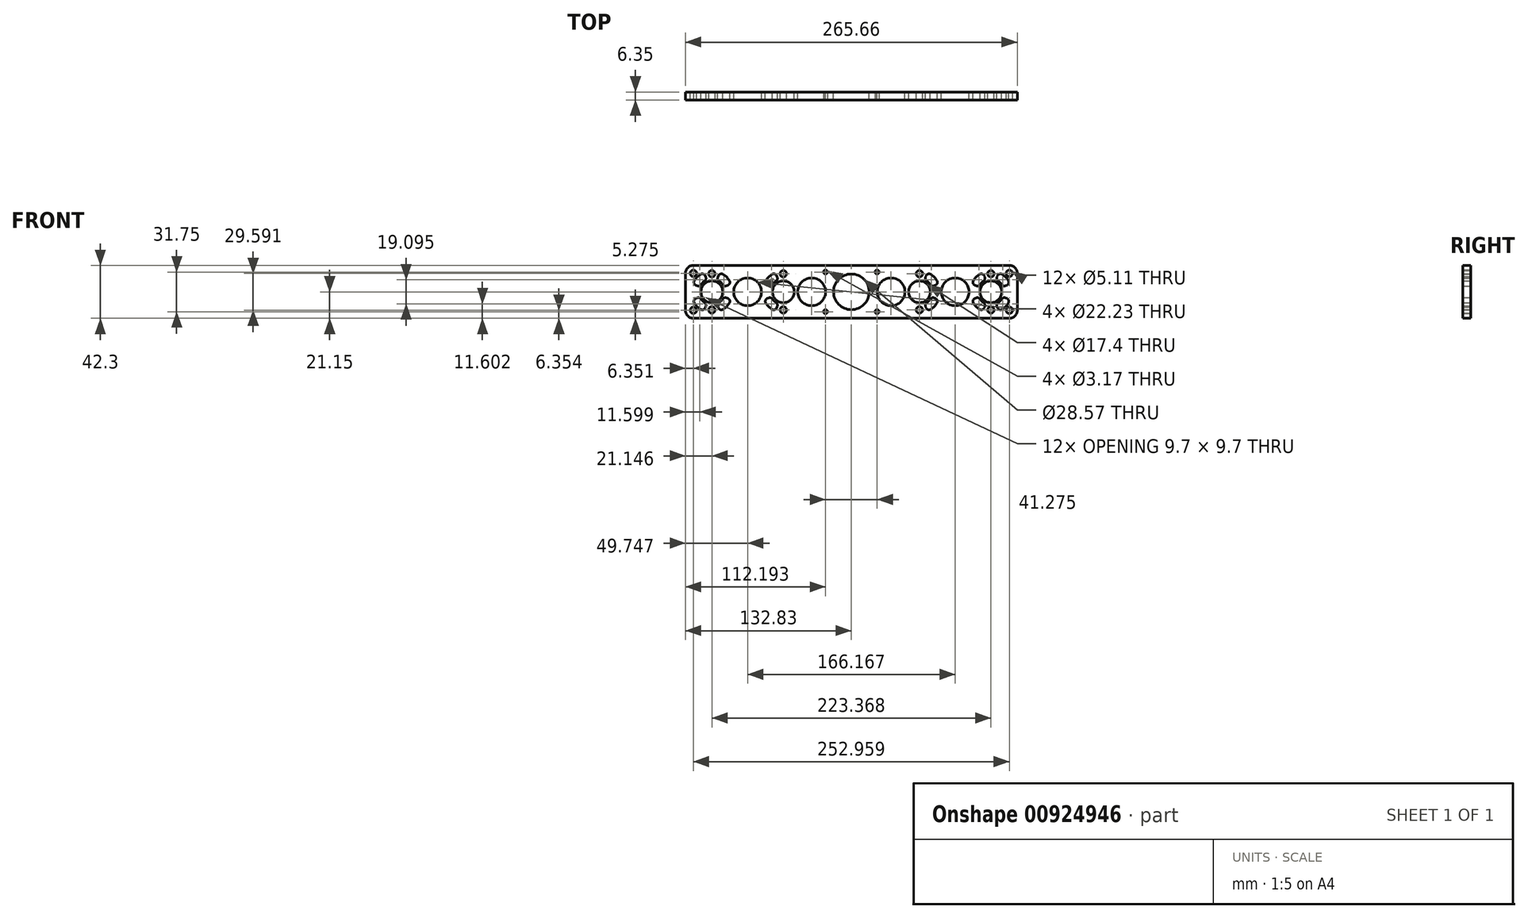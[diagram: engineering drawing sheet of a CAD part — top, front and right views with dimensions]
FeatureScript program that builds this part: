
annotation { "Feature Type Name" : "Feature", "Feature Type Description" : "" }
export const myFeature = defineFeature(function(context is Context, id is Id, definition is map)
    precondition{}
    {
        {
            var Q0;
            Q0=qCreatedBy(makeId("Front.planeOp"),FACE);
            var sketch = newSketch(context, id + "F0", { "sketchPlane" : qUnion([Q0])});
            skLineSegment(sketch, "E0.bottom", {"start": v(-139.7, 25.4) * mm, "end": v(139.7, 25.4) * mm, "construction": true});
            skLineSegment(sketch, "E0.top", {"start": v(-139.7, -25.4) * mm, "end": v(139.7, -25.4) * mm, "construction": true});
            skLineSegment(sketch, "E0.left", {"start": v(-139.7, 25.4) * mm, "end": v(-139.7, -25.4) * mm, "construction": true});
            skLineSegment(sketch, "E0.right", {"start": v(139.7, 25.4) * mm, "end": v(139.7, -25.4) * mm, "construction": true});
            skPoint(sketch, "E0.middle", {"position": v(0, 0) * mm});
            skCircle(sketch, "E1", {"center": v(-111.68, 0) * mm, "radius": 21.15 * mm, "construction": true});
            skCircle(sketch, "E2", {"center": v(-54.48, 0) * mm, "radius": 21.15 * mm, "construction": true});
            skCircle(sketch, "E3", {"center": v(-111.68, 0) * mm, "radius": 4.78 * mm, "construction": true});
            skCircle(sketch, "E4", {"center": v(-83.08, 0) * mm, "radius": 23.83 * mm, "construction": true});
            skCircle(sketch, "E5", {"center": v(-54.48, 0) * mm, "radius": 4.78 * mm, "construction": true});
            skCircle(sketch, "E6", {"center": v(-83.08, 0) * mm, "radius": 19.09 * mm, "construction": true});
            skCircle(sketch, "E7", {"center": v(-31.78, 0) * mm, "radius": 19.09 * mm, "construction": true});
            skCircle(sketch, "E8", {"center": v(-83.08, 0) * mm, "radius": 11.11 * mm});
            skCircle(sketch, "E9", {"center": v(-31.78, 0) * mm, "radius": 8.9 * mm, "construction": true});
            skCircle(sketch, "E10", {"center": v(0, 0) * mm, "radius": 22.87 * mm, "construction": true});
            skLineSegment(sketch, "E11", {"start": v(0, 25.4) * mm, "end": v(0, -25.4) * mm, "construction": true});
            skCircle(sketch, "E12.MirrorC", {"center": v(54.48, 0) * mm, "radius": 21.15 * mm, "construction": true});
            skCircle(sketch, "E13.MirrorC", {"center": v(111.68, 0) * mm, "radius": 21.15 * mm, "construction": true});
            skCircle(sketch, "E14.MirrorC", {"center": v(111.68, 0) * mm, "radius": 4.78 * mm, "construction": true});
            skCircle(sketch, "E15.MirrorC", {"center": v(83.08, 0) * mm, "radius": 19.09 * mm, "construction": true});
            skCircle(sketch, "E16.MirrorC", {"center": v(83.08, 0) * mm, "radius": 11.11 * mm});
            skCircle(sketch, "E17.MirrorC", {"center": v(54.48, 0) * mm, "radius": 4.78 * mm, "construction": true});
            skCircle(sketch, "E18.MirrorC", {"center": v(83.08, 0) * mm, "radius": 23.83 * mm, "construction": true});
            skCircle(sketch, "E19.MirrorC", {"center": v(31.78, 0) * mm, "radius": 19.09 * mm, "construction": true});
            skCircle(sketch, "E20.MirrorC", {"center": v(31.78, 0) * mm, "radius": 8.9 * mm, "construction": true});
            skLineSegment(sketch, "E21", {"start": v(-111.68, 14.5) * mm, "end": v(-111.68, 0) * mm, "construction": true});
            skLineSegment(sketch, "E22", {"start": v(-111.68, 0) * mm, "end": v(-111.68, -14.5) * mm, "construction": true});
            skCircle(sketch, "E23", {"center": v(-111.68, 14.5) * mm, "radius": 2.55 * mm});
            skCircle(sketch, "E24", {"center": v(-111.68, -14.5) * mm, "radius": 2.55 * mm});
            skCircle(sketch, "E25", {"center": v(-111.68, 0) * mm, "radius": 8.7 * mm});
            skLineSegment(sketch, "E26", {"start": v(-54.48, -14.5) * mm, "end": v(-54.48, 0) * mm, "construction": true});
            skLineSegment(sketch, "E27", {"start": v(-54.48, 0) * mm, "end": v(-54.48, 14.5) * mm, "construction": true});
            skCircle(sketch, "E28", {"center": v(-54.48, 14.5) * mm, "radius": 2.55 * mm});
            skCircle(sketch, "E29", {"center": v(-54.48, -14.5) * mm, "radius": 2.55 * mm});
            skCircle(sketch, "E30", {"center": v(-54.48, 0) * mm, "radius": 8.7 * mm});
            skLineSegment(sketch, "E31.MirrorCS", {"start": v(54.48, 0) * mm, "end": v(54.48, 14.5) * mm, "construction": true});
            skCircle(sketch, "E32.MirrorC", {"center": v(54.48, 14.5) * mm, "radius": 2.55 * mm});
            skLineSegment(sketch, "E33.MirrorCS", {"start": v(54.48, -14.5) * mm, "end": v(54.48, 0) * mm, "construction": true});
            skCircle(sketch, "E34.MirrorC", {"center": v(54.48, -14.5) * mm, "radius": 2.55 * mm});
            skCircle(sketch, "E35.MirrorC", {"center": v(54.48, 0) * mm, "radius": 8.7 * mm});
            skCircle(sketch, "E36.MirrorC", {"center": v(111.68, 0) * mm, "radius": 8.7 * mm});
            skLineSegment(sketch, "E37.MirrorCS", {"start": v(111.68, 0) * mm, "end": v(111.68, -14.5) * mm, "construction": true});
            skCircle(sketch, "E38.MirrorC", {"center": v(111.68, -14.5) * mm, "radius": 2.55 * mm});
            skLineSegment(sketch, "E39.MirrorCS", {"start": v(111.68, 14.5) * mm, "end": v(111.68, 0) * mm, "construction": true});
            skCircle(sketch, "E40.MirrorC", {"center": v(111.68, 14.5) * mm, "radius": 2.55 * mm});
            skCircle(sketch, "E41", {"center": v(-31.78, 0) * mm, "radius": 11.11 * mm});
            skCircle(sketch, "E42", {"center": v(31.78, 0) * mm, "radius": 11.11 * mm});
            skCircle(sketch, "E43", {"center": v(0, 0) * mm, "radius": 14.29 * mm});
            skArc(sketch, "E44", {"start": v(-111.68, 21.15) * mm, "mid": v(-132.83, 0) * mm, "end": v(-111.68, -21.15) * mm, "construction": true});
            skLineSegment(sketch, "E45", {"start": v(-111.68, 21.15) * mm, "end": v(111.68, 21.15) * mm});
            skArc(sketch, "E46", {"start": v(111.68, 21.15) * mm, "mid": v(132.83, 0) * mm, "end": v(111.68, -21.15) * mm, "construction": true});
            skLineSegment(sketch, "E47", {"start": v(111.68, -21.15) * mm, "end": v(-111.68, -21.15) * mm});
            skLineSegment(sketch, "E48", {"start": v(111.68, 21.15) * mm, "end": v(126.48, 21.15) * mm});
            skPoint(sketch, "E48.endSnap0", {"position": v(132.83, 0) * mm});
            skLineSegment(sketch, "E49", {"start": v(132.83, 14.8) * mm, "end": v(132.83, -14.8) * mm});
            skLineSegment(sketch, "E50", {"start": v(126.48, -21.15) * mm, "end": v(111.68, -21.15) * mm});
            skCircle(sketch, "E51", {"center": v(126.48, 14.8) * mm, "radius": 6.35 * mm, "construction": true});
            skCircle(sketch, "E52", {"center": v(126.48, 14.8) * mm, "radius": 2.55 * mm});
            skLineSegment(sketch, "E53", {"start": v(-111.68, -21.15) * mm, "end": v(-126.48, -21.15) * mm});
            skPoint(sketch, "E53.endSnap0", {"position": v(-132.83, 0) * mm});
            skLineSegment(sketch, "E54", {"start": v(-132.83, -14.8) * mm, "end": v(-132.83, 14.8) * mm});
            skLineSegment(sketch, "E55", {"start": v(-126.48, 21.15) * mm, "end": v(-111.68, 21.15) * mm});
            skPoint(sketch, "E56.visualSharp", {"position": v(132.83, 21.15) * mm});
            skArc(sketch, "E56.filletArc", {"start": v(132.83, 14.8) * mm, "mid": v(130.97, 19.29) * mm, "end": v(126.48, 21.15) * mm});
            skPoint(sketch, "E57.visualSharp", {"position": v(132.83, -21.15) * mm});
            skArc(sketch, "E57.filletArc", {"start": v(126.48, -21.15) * mm, "mid": v(130.97, -19.29) * mm, "end": v(132.83, -14.8) * mm});
            skPoint(sketch, "E58.visualSharp", {"position": v(-132.83, -21.15) * mm});
            skArc(sketch, "E58.filletArc", {"start": v(-132.83, -14.8) * mm, "mid": v(-130.97, -19.29) * mm, "end": v(-126.48, -21.15) * mm});
            skPoint(sketch, "E59.visualSharp", {"position": v(-132.83, 21.15) * mm});
            skArc(sketch, "E59.filletArc", {"start": v(-126.48, 21.15) * mm, "mid": v(-130.97, 19.29) * mm, "end": v(-132.83, 14.8) * mm});
            skCircle(sketch, "E60", {"center": v(-126.48, 14.8) * mm, "radius": 6.35 * mm, "construction": true});
            skCircle(sketch, "E61", {"center": v(126.48, -14.8) * mm, "radius": 6.35 * mm, "construction": true});
            skCircle(sketch, "E62", {"center": v(126.48, -14.8) * mm, "radius": 2.55 * mm});
            skCircle(sketch, "E63", {"center": v(-126.48, -14.8) * mm, "radius": 6.35 * mm, "construction": true});
            skCircle(sketch, "E64", {"center": v(-126.48, -14.8) * mm, "radius": 2.55 * mm});
            skCircle(sketch, "E65", {"center": v(-126.48, 14.8) * mm, "radius": 2.55 * mm});
            skSolve(sketch);
        }
        {
            var Q0;
            Q0 = qSketchRegion(id + "F0", true);
            extrude(context, id + "F1", {"entities" : qUnion([Q0]), "depth" : 6.35 * mm, "offsetDistance" : 25.4 * mm});
        }
        {
            var Q0;
            Q0=makeQuery(id+"F1.opExtrude","CAP_FACE",FACE,{"disambiguationData":[OSD([sQuery(id+"F0.wireOp",EDGE,"E8"),sQuery(id+"F0.wireOp",EDGE,"E16.MirrorC"),sQuery(id+"F0.wireOp",EDGE,"E23"),sQuery(id+"F0.wireOp",EDGE,"E24"),sQuery(id+"F0.wireOp",EDGE,"E25"),sQuery(id+"F0.wireOp",EDGE,"E28"),sQuery(id+"F0.wireOp",EDGE,"E29"),sQuery(id+"F0.wireOp",EDGE,"E30"),sQuery(id+"F0.wireOp",EDGE,"E32.MirrorC"),sQuery(id+"F0.wireOp",EDGE,"E34.MirrorC"),sQuery(id+"F0.wireOp",EDGE,"E35.MirrorC"),sQuery(id+"F0.wireOp",EDGE,"E36.MirrorC"),sQuery(id+"F0.wireOp",EDGE,"E38.MirrorC"),sQuery(id+"F0.wireOp",EDGE,"E40.MirrorC"),sQuery(id+"F0.wireOp",EDGE,"E41"),sQuery(id+"F0.wireOp",EDGE,"E42"),sQuery(id+"F0.wireOp",EDGE,"E43"),sQuery(id+"F0.wireOp",EDGE,"E44"),sQuery(id+"F0.wireOp",EDGE,"E45"),sQuery(id+"F0.wireOp",EDGE,"E46"),sQuery(id+"F0.wireOp",EDGE,"E47")])],"isStart":false});
            var sketch = newSketch(context, id + "F2", { "sketchPlane" : qUnion([Q0])});
            skLineSegment(sketch, "E66.bottom", {"start": v(20.64, 15.88) * mm, "end": v(-20.64, 15.88) * mm, "construction": true});
            skLineSegment(sketch, "E66.top", {"start": v(20.64, -15.88) * mm, "end": v(-20.64, -15.88) * mm, "construction": true});
            skLineSegment(sketch, "E66.left", {"start": v(20.64, 15.88) * mm, "end": v(20.64, -15.88) * mm, "construction": true});
            skLineSegment(sketch, "E66.right", {"start": v(-20.64, 15.88) * mm, "end": v(-20.64, -15.88) * mm, "construction": true});
            skPoint(sketch, "E66.middle", {"position": v(0, 0) * mm});
            skCircle(sketch, "E67", {"center": v(20.64, 15.88) * mm, "radius": 1.59 * mm});
            skCircle(sketch, "E68", {"center": v(20.64, -15.88) * mm, "radius": 1.59 * mm});
            skCircle(sketch, "E69", {"center": v(-20.64, -15.88) * mm, "radius": 1.59 * mm});
            skCircle(sketch, "E70", {"center": v(-20.64, 15.88) * mm, "radius": 1.59 * mm});
            skSolve(sketch);
        }
        {
            var Q0;
            Q0 = qSketchRegion(id + "F2", true);
            extrude(context, id + "F3", {"entities" : qUnion([Q0]), "operationType" : NewBodyOperationType.REMOVE, "endBound" : BoundingType.THROUGH_ALL, "oppositeDirection" : true, "depth" : 25.4 * mm, "offsetDistance" : 25.4 * mm});
        }
        {
            var Q0;
            Q0=makeQuery(id+"F1.opExtrude","CAP_FACE",FACE,{"disambiguationData":[OSD([sQuery(id+"F0.wireOp",EDGE,"E8"),sQuery(id+"F0.wireOp",EDGE,"E16.MirrorC"),sQuery(id+"F0.wireOp",EDGE,"E23"),sQuery(id+"F0.wireOp",EDGE,"E24"),sQuery(id+"F0.wireOp",EDGE,"E25"),sQuery(id+"F0.wireOp",EDGE,"E28"),sQuery(id+"F0.wireOp",EDGE,"E29"),sQuery(id+"F0.wireOp",EDGE,"E30"),sQuery(id+"F0.wireOp",EDGE,"E32.MirrorC"),sQuery(id+"F0.wireOp",EDGE,"E34.MirrorC"),sQuery(id+"F0.wireOp",EDGE,"E35.MirrorC"),sQuery(id+"F0.wireOp",EDGE,"E36.MirrorC"),sQuery(id+"F0.wireOp",EDGE,"E38.MirrorC"),sQuery(id+"F0.wireOp",EDGE,"E40.MirrorC"),sQuery(id+"F0.wireOp",EDGE,"E41"),sQuery(id+"F0.wireOp",EDGE,"E42"),sQuery(id+"F0.wireOp",EDGE,"E43"),sQuery(id+"F0.wireOp",EDGE,"E45"),sQuery(id+"F0.wireOp",EDGE,"E47"),sQuery(id+"F0.wireOp",EDGE,"E48"),sQuery(id+"F0.wireOp",EDGE,"E49"),sQuery(id+"F0.wireOp",EDGE,"E50"),sQuery(id+"F0.wireOp",EDGE,"E52"),sQuery(id+"F0.wireOp",EDGE,"E53"),sQuery(id+"F0.wireOp",EDGE,"E54"),sQuery(id+"F0.wireOp",EDGE,"E55"),sQuery(id+"F0.wireOp",EDGE,"E56.filletArc"),sQuery(id+"F0.wireOp",EDGE,"E57.filletArc"),sQuery(id+"F0.wireOp",EDGE,"E58.filletArc"),sQuery(id+"F0.wireOp",EDGE,"E59.filletArc"),sQuery(id+"F0.wireOp",EDGE,"E62"),sQuery(id+"F0.wireOp",EDGE,"E64"),sQuery(id+"F0.wireOp",EDGE,"E65")])],"isStart":true});
            var sketch = newSketch(context, id + "F4", { "sketchPlane" : qUnion([Q0])});
            skCircle(sketch, "E71", {"center": v(111.68, 0) * mm, "radius": 10.48 * mm, "construction": true});
            skCircle(sketch, "E72", {"center": v(111.68, 0) * mm, "radius": 16.67 * mm, "construction": true});
            skLineSegment(sketch, "E73", {"start": v(118.06, 15.4) * mm, "end": v(105.3, -15.4) * mm, "construction": true});
            skLineSegment(sketch, "E74", {"start": v(105.3, 15.4) * mm, "end": v(118.06, -15.4) * mm, "construction": true});
            skLineSegment(sketch, "E75", {"start": v(96.28, 6.38) * mm, "end": v(127.08, -6.38) * mm, "construction": true});
            skLineSegment(sketch, "E76", {"start": v(127.08, 6.38) * mm, "end": v(96.28, -6.38) * mm, "construction": true});
            skLineSegment(sketch, "E77", {"start": v(95.02, 0) * mm, "end": v(128.35, 0) * mm, "construction": true});
            skLineSegment(sketch, "E78", {"start": v(106.8, -11.8) * mm, "end": v(106.37, -12.84) * mm});
            skLineSegment(sketch, "E79", {"start": v(99.89, -4.89) * mm, "end": v(98.84, -5.32) * mm});
            skLineSegment(sketch, "E80", {"start": v(99.89, 4.89) * mm, "end": v(98.84, 5.32) * mm});
            skLineSegment(sketch, "E81", {"start": v(106.8, 11.8) * mm, "end": v(106.37, 12.84) * mm});
            skLineSegment(sketch, "E82", {"start": v(116.57, 11.8) * mm, "end": v(117, 12.84) * mm});
            skLineSegment(sketch, "E83", {"start": v(123.48, 4.89) * mm, "end": v(124.52, 5.32) * mm});
            skLineSegment(sketch, "E84", {"start": v(122.16, 0) * mm, "end": v(128.35, 0) * mm});
            skLineSegment(sketch, "E85", {"start": v(123.48, -4.89) * mm, "end": v(124.52, -5.32) * mm});
            skLineSegment(sketch, "E86", {"start": v(116.57, -11.8) * mm, "end": v(117, -12.84) * mm});
            skArc(sketch, "E87", {"start": v(120.73, -14) * mm, "mid": v(123.47, -11.79) * mm, "end": v(125.69, -9.04) * mm});
            skArc(sketch, "E88", {"start": v(125.69, 9.04) * mm, "mid": v(123.47, 11.79) * mm, "end": v(120.73, 14) * mm});
            skArc(sketch, "E89", {"start": v(102.64, 14) * mm, "mid": v(99.9, 11.79) * mm, "end": v(97.68, 9.04) * mm});
            skArc(sketch, "E90", {"start": v(97.68, -9.04) * mm, "mid": v(99.9, -11.79) * mm, "end": v(102.64, -14) * mm});
            skArc(sketch, "E91", {"start": v(120.4, -5.82) * mm, "mid": v(119.1, -7.4) * mm, "end": v(117.5, -8.71) * mm});
            skArc(sketch, "E92", {"start": v(105.86, -8.71) * mm, "mid": v(104.28, -7.4) * mm, "end": v(102.97, -5.82) * mm});
            skArc(sketch, "E93", {"start": v(102.97, 5.82) * mm, "mid": v(104.28, 7.4) * mm, "end": v(105.86, 8.71) * mm});
            skArc(sketch, "E94", {"start": v(117.5, 8.71) * mm, "mid": v(119.1, 7.4) * mm, "end": v(120.4, 5.82) * mm});
            skPoint(sketch, "E95.visualSharp", {"position": v(115.7, -9.68) * mm});
            skArc(sketch, "E95.filletArc", {"start": v(117.5, -8.71) * mm, "mid": v(116.49, -10.09) * mm, "end": v(116.57, -11.8) * mm});
            skPoint(sketch, "E96.visualSharp", {"position": v(118.06, -15.4) * mm});
            skArc(sketch, "E96.filletArc", {"start": v(117, -12.84) * mm, "mid": v(118.6, -14.3) * mm, "end": v(120.73, -14) * mm});
            skPoint(sketch, "E97.visualSharp", {"position": v(127.08, -6.38) * mm});
            skArc(sketch, "E97.filletArc", {"start": v(125.69, -9.04) * mm, "mid": v(125.98, -6.9) * mm, "end": v(124.52, -5.32) * mm});
            skPoint(sketch, "E98.visualSharp", {"position": v(121.36, -4) * mm});
            skArc(sketch, "E98.filletArc", {"start": v(123.48, -4.89) * mm, "mid": v(121.77, -4.8) * mm, "end": v(120.4, -5.82) * mm});
            skPoint(sketch, "E99.visualSharp", {"position": v(121.36, 4) * mm});
            skArc(sketch, "E99.filletArc", {"start": v(120.4, 5.82) * mm, "mid": v(121.77, 4.8) * mm, "end": v(123.48, 4.89) * mm});
            skPoint(sketch, "E100.visualSharp", {"position": v(127.08, 6.38) * mm});
            skArc(sketch, "E100.filletArc", {"start": v(124.52, 5.32) * mm, "mid": v(125.98, 6.9) * mm, "end": v(125.69, 9.04) * mm});
            skPoint(sketch, "E101.visualSharp", {"position": v(118.06, 15.4) * mm});
            skArc(sketch, "E101.filletArc", {"start": v(120.73, 14) * mm, "mid": v(118.6, 14.3) * mm, "end": v(117, 12.84) * mm});
            skPoint(sketch, "E102.visualSharp", {"position": v(115.7, 9.68) * mm});
            skArc(sketch, "E102.filletArc", {"start": v(116.57, 11.8) * mm, "mid": v(116.49, 10.09) * mm, "end": v(117.5, 8.71) * mm});
            skPoint(sketch, "E103.visualSharp", {"position": v(107.67, 9.68) * mm});
            skArc(sketch, "E103.filletArc", {"start": v(105.86, 8.71) * mm, "mid": v(106.88, 10.09) * mm, "end": v(106.8, 11.8) * mm});
            skPoint(sketch, "E104.visualSharp", {"position": v(105.3, 15.4) * mm});
            skArc(sketch, "E104.filletArc", {"start": v(106.37, 12.84) * mm, "mid": v(104.77, 14.3) * mm, "end": v(102.64, 14) * mm});
            skPoint(sketch, "E105.visualSharp", {"position": v(96.28, 6.38) * mm});
            skArc(sketch, "E105.filletArc", {"start": v(97.68, 9.04) * mm, "mid": v(97.4, 6.9) * mm, "end": v(98.84, 5.32) * mm});
            skPoint(sketch, "E106.visualSharp", {"position": v(102, 4) * mm});
            skArc(sketch, "E106.filletArc", {"start": v(99.89, 4.89) * mm, "mid": v(101.6, 4.8) * mm, "end": v(102.97, 5.82) * mm});
            skPoint(sketch, "E107.visualSharp", {"position": v(102, -4) * mm});
            skArc(sketch, "E107.filletArc", {"start": v(102.97, -5.82) * mm, "mid": v(101.6, -4.8) * mm, "end": v(99.89, -4.89) * mm});
            skPoint(sketch, "E108.visualSharp", {"position": v(107.67, -9.68) * mm});
            skArc(sketch, "E108.filletArc", {"start": v(106.8, -11.8) * mm, "mid": v(106.88, -10.09) * mm, "end": v(105.86, -8.71) * mm});
            skPoint(sketch, "E109.visualSharp", {"position": v(105.3, -15.4) * mm});
            skArc(sketch, "E109.filletArc", {"start": v(102.64, -14) * mm, "mid": v(104.77, -14.3) * mm, "end": v(106.37, -12.84) * mm});
            skPoint(sketch, "E110.visualSharp", {"position": v(96.28, -6.38) * mm});
            skArc(sketch, "E110.filletArc", {"start": v(98.84, -5.32) * mm, "mid": v(97.4, -6.9) * mm, "end": v(97.68, -9.04) * mm});
            skLineSegment(sketch, "E111", {"start": v(54.48, -14.5) * mm, "end": v(54.48, 14.5) * mm, "construction": true});
            skLineSegment(sketch, "E112", {"start": v(-54.48, -14.5) * mm, "end": v(-54.48, 14.5) * mm, "construction": true});
            skLineSegment(sketch, "E113", {"start": v(-111.68, 14.5) * mm, "end": v(-111.68, -14.5) * mm, "construction": true});
            skCircle(sketch, "E114", {"center": v(54.48, 0) * mm, "radius": 10.48 * mm, "construction": true});
            skCircle(sketch, "E115", {"center": v(54.48, 0) * mm, "radius": 16.67 * mm, "construction": true});
            skLineSegment(sketch, "E116", {"start": v(60.86, 15.4) * mm, "end": v(48.1, -15.4) * mm, "construction": true});
            skLineSegment(sketch, "E117", {"start": v(48.1, 15.4) * mm, "end": v(60.86, -15.4) * mm, "construction": true});
            skLineSegment(sketch, "E118", {"start": v(39.08, 6.38) * mm, "end": v(69.88, -6.38) * mm, "construction": true});
            skLineSegment(sketch, "E119", {"start": v(69.88, 6.38) * mm, "end": v(39.08, -6.38) * mm, "construction": true});
            skLineSegment(sketch, "E120", {"start": v(37.81, 0) * mm, "end": v(71.15, 0) * mm, "construction": true});
            skLineSegment(sketch, "E121", {"start": v(49.6, -11.8) * mm, "end": v(49.16, -12.84) * mm, "construction": true});
            skLineSegment(sketch, "E122", {"start": v(42.69, -4.89) * mm, "end": v(41.64, -5.32) * mm, "construction": true});
            skLineSegment(sketch, "E123", {"start": v(42.69, 4.89) * mm, "end": v(41.64, 5.32) * mm, "construction": true});
            skLineSegment(sketch, "E124", {"start": v(49.6, 11.8) * mm, "end": v(49.16, 12.84) * mm, "construction": true});
            skLineSegment(sketch, "E125", {"start": v(59.37, 11.8) * mm, "end": v(59.8, 12.84) * mm});
            skLineSegment(sketch, "E126", {"start": v(66.28, 4.89) * mm, "end": v(67.32, 5.32) * mm});
            skLineSegment(sketch, "E127", {"start": v(64.96, 0) * mm, "end": v(71.15, 0) * mm});
            skLineSegment(sketch, "E128", {"start": v(66.28, -4.89) * mm, "end": v(67.32, -5.32) * mm});
            skLineSegment(sketch, "E129", {"start": v(59.37, -11.8) * mm, "end": v(59.8, -12.84) * mm});
            skArc(sketch, "E130", {"start": v(63.53, -14) * mm, "mid": v(66.27, -11.79) * mm, "end": v(68.49, -9.04) * mm});
            skArc(sketch, "E131", {"start": v(68.49, 9.04) * mm, "mid": v(66.27, 11.79) * mm, "end": v(63.53, 14) * mm});
            skArc(sketch, "E132", {"start": v(45.44, 14) * mm, "mid": v(42.7, 11.79) * mm, "end": v(40.48, 9.04) * mm, "construction": true});
            skArc(sketch, "E133", {"start": v(40.48, -9.04) * mm, "mid": v(42.7, -11.79) * mm, "end": v(45.44, -14) * mm, "construction": true});
            skArc(sketch, "E134", {"start": v(63.2, -5.82) * mm, "mid": v(61.9, -7.4) * mm, "end": v(60.3, -8.71) * mm});
            skArc(sketch, "E135", {"start": v(48.66, -8.71) * mm, "mid": v(47.07, -7.4) * mm, "end": v(45.77, -5.82) * mm, "construction": true});
            skArc(sketch, "E136", {"start": v(45.77, 5.82) * mm, "mid": v(47.07, 7.4) * mm, "end": v(48.66, 8.71) * mm, "construction": true});
            skArc(sketch, "E137", {"start": v(60.3, 8.71) * mm, "mid": v(61.9, 7.4) * mm, "end": v(63.2, 5.82) * mm});
            skPoint(sketch, "E138.visualSharp", {"position": v(58.5, -9.68) * mm});
            skArc(sketch, "E138.filletArc", {"start": v(60.3, -8.71) * mm, "mid": v(59.28, -10.09) * mm, "end": v(59.37, -11.8) * mm});
            skPoint(sketch, "E139.visualSharp", {"position": v(60.86, -15.4) * mm});
            skArc(sketch, "E139.filletArc", {"start": v(59.8, -12.84) * mm, "mid": v(61.4, -14.3) * mm, "end": v(63.53, -14) * mm});
            skPoint(sketch, "E140.visualSharp", {"position": v(69.88, -6.38) * mm});
            skArc(sketch, "E140.filletArc", {"start": v(68.49, -9.04) * mm, "mid": v(68.78, -6.9) * mm, "end": v(67.32, -5.32) * mm});
            skPoint(sketch, "E141.visualSharp", {"position": v(64.16, -4) * mm});
            skArc(sketch, "E141.filletArc", {"start": v(66.28, -4.89) * mm, "mid": v(64.57, -4.8) * mm, "end": v(63.2, -5.82) * mm});
            skPoint(sketch, "E142.visualSharp", {"position": v(64.16, 4) * mm});
            skArc(sketch, "E142.filletArc", {"start": v(63.2, 5.82) * mm, "mid": v(64.57, 4.8) * mm, "end": v(66.28, 4.89) * mm});
            skPoint(sketch, "E143.visualSharp", {"position": v(69.88, 6.38) * mm});
            skArc(sketch, "E143.filletArc", {"start": v(67.32, 5.32) * mm, "mid": v(68.78, 6.9) * mm, "end": v(68.49, 9.04) * mm});
            skPoint(sketch, "E144.visualSharp", {"position": v(60.86, 15.4) * mm});
            skArc(sketch, "E144.filletArc", {"start": v(63.53, 14) * mm, "mid": v(61.4, 14.3) * mm, "end": v(59.8, 12.84) * mm});
            skPoint(sketch, "E145.visualSharp", {"position": v(58.5, 9.68) * mm});
            skArc(sketch, "E145.filletArc", {"start": v(59.37, 11.8) * mm, "mid": v(59.28, 10.09) * mm, "end": v(60.3, 8.71) * mm});
            skPoint(sketch, "E146.visualSharp", {"position": v(50.47, 9.68) * mm});
            skArc(sketch, "E146.filletArc", {"start": v(48.66, 8.71) * mm, "mid": v(49.68, 10.09) * mm, "end": v(49.6, 11.8) * mm, "construction": true});
            skPoint(sketch, "E147.visualSharp", {"position": v(48.1, 15.4) * mm});
            skArc(sketch, "E147.filletArc", {"start": v(49.16, 12.84) * mm, "mid": v(47.57, 14.3) * mm, "end": v(45.44, 14) * mm, "construction": true});
            skPoint(sketch, "E148.visualSharp", {"position": v(39.08, 6.38) * mm});
            skArc(sketch, "E148.filletArc", {"start": v(40.48, 9.04) * mm, "mid": v(40.19, 6.9) * mm, "end": v(41.64, 5.32) * mm, "construction": true});
            skPoint(sketch, "E149.visualSharp", {"position": v(44.8, 4) * mm});
            skArc(sketch, "E149.filletArc", {"start": v(42.69, 4.89) * mm, "mid": v(44.4, 4.8) * mm, "end": v(45.77, 5.82) * mm, "construction": true});
            skPoint(sketch, "E150.visualSharp", {"position": v(44.8, -4) * mm});
            skArc(sketch, "E150.filletArc", {"start": v(45.77, -5.82) * mm, "mid": v(44.4, -4.8) * mm, "end": v(42.69, -4.89) * mm, "construction": true});
            skPoint(sketch, "E151.visualSharp", {"position": v(50.47, -9.68) * mm});
            skArc(sketch, "E151.filletArc", {"start": v(49.6, -11.8) * mm, "mid": v(49.68, -10.09) * mm, "end": v(48.66, -8.71) * mm, "construction": true});
            skPoint(sketch, "E152.visualSharp", {"position": v(48.1, -15.4) * mm});
            skArc(sketch, "E152.filletArc", {"start": v(45.44, -14) * mm, "mid": v(47.57, -14.3) * mm, "end": v(49.16, -12.84) * mm, "construction": true});
            skPoint(sketch, "E153.visualSharp", {"position": v(39.08, -6.38) * mm});
            skArc(sketch, "E153.filletArc", {"start": v(41.64, -5.32) * mm, "mid": v(40.19, -6.9) * mm, "end": v(40.48, -9.04) * mm, "construction": true});
            skCircle(sketch, "E154", {"center": v(-54.48, 0) * mm, "radius": 10.48 * mm, "construction": true});
            skCircle(sketch, "E155", {"center": v(-54.48, 0) * mm, "radius": 16.67 * mm, "construction": true});
            skLineSegment(sketch, "E156", {"start": v(-48.1, 15.4) * mm, "end": v(-60.86, -15.4) * mm, "construction": true});
            skLineSegment(sketch, "E157", {"start": v(-60.86, 15.4) * mm, "end": v(-48.1, -15.4) * mm, "construction": true});
            skLineSegment(sketch, "E158", {"start": v(-69.88, 6.38) * mm, "end": v(-39.08, -6.38) * mm, "construction": true});
            skLineSegment(sketch, "E159", {"start": v(-39.08, 6.38) * mm, "end": v(-69.88, -6.38) * mm, "construction": true});
            skLineSegment(sketch, "E160", {"start": v(-71.15, 0) * mm, "end": v(-37.81, 0) * mm, "construction": true});
            skLineSegment(sketch, "E161", {"start": v(-59.37, -11.8) * mm, "end": v(-59.8, -12.84) * mm});
            skLineSegment(sketch, "E162", {"start": v(-66.28, -4.89) * mm, "end": v(-67.32, -5.32) * mm});
            skLineSegment(sketch, "E163", {"start": v(-66.28, 4.89) * mm, "end": v(-67.32, 5.32) * mm});
            skLineSegment(sketch, "E164", {"start": v(-59.37, 11.8) * mm, "end": v(-59.8, 12.84) * mm});
            skLineSegment(sketch, "E165", {"start": v(-49.6, 11.8) * mm, "end": v(-49.16, 12.84) * mm, "construction": true});
            skLineSegment(sketch, "E166", {"start": v(-42.69, 4.89) * mm, "end": v(-41.64, 5.32) * mm, "construction": true});
            skLineSegment(sketch, "E167", {"start": v(-44, 0) * mm, "end": v(-37.81, 0) * mm, "construction": true});
            skLineSegment(sketch, "E168", {"start": v(-42.69, -4.89) * mm, "end": v(-41.64, -5.32) * mm, "construction": true});
            skLineSegment(sketch, "E169", {"start": v(-49.6, -11.8) * mm, "end": v(-49.16, -12.84) * mm, "construction": true});
            skArc(sketch, "E170", {"start": v(-45.44, -14) * mm, "mid": v(-42.7, -11.79) * mm, "end": v(-40.48, -9.04) * mm, "construction": true});
            skArc(sketch, "E171", {"start": v(-40.48, 9.04) * mm, "mid": v(-42.7, 11.79) * mm, "end": v(-45.44, 14) * mm, "construction": true});
            skArc(sketch, "E172", {"start": v(-63.53, 14) * mm, "mid": v(-66.27, 11.79) * mm, "end": v(-68.49, 9.04) * mm});
            skArc(sketch, "E173", {"start": v(-68.49, -9.04) * mm, "mid": v(-66.27, -11.79) * mm, "end": v(-63.53, -14) * mm});
            skArc(sketch, "E174", {"start": v(-45.77, -5.82) * mm, "mid": v(-47.07, -7.4) * mm, "end": v(-48.66, -8.71) * mm, "construction": true});
            skArc(sketch, "E175", {"start": v(-60.3, -8.71) * mm, "mid": v(-61.9, -7.4) * mm, "end": v(-63.2, -5.82) * mm});
            skArc(sketch, "E176", {"start": v(-63.2, 5.82) * mm, "mid": v(-61.9, 7.4) * mm, "end": v(-60.3, 8.71) * mm});
            skArc(sketch, "E177", {"start": v(-48.66, 8.71) * mm, "mid": v(-47.07, 7.4) * mm, "end": v(-45.77, 5.82) * mm, "construction": true});
            skPoint(sketch, "E178.visualSharp", {"position": v(-50.47, -9.68) * mm});
            skArc(sketch, "E178.filletArc", {"start": v(-48.66, -8.71) * mm, "mid": v(-49.68, -10.09) * mm, "end": v(-49.6, -11.8) * mm, "construction": true});
            skPoint(sketch, "E179.visualSharp", {"position": v(-48.1, -15.4) * mm});
            skArc(sketch, "E179.filletArc", {"start": v(-49.16, -12.84) * mm, "mid": v(-47.57, -14.3) * mm, "end": v(-45.44, -14) * mm, "construction": true});
            skPoint(sketch, "E180.visualSharp", {"position": v(-39.08, -6.38) * mm});
            skArc(sketch, "E180.filletArc", {"start": v(-40.48, -9.04) * mm, "mid": v(-40.19, -6.9) * mm, "end": v(-41.64, -5.32) * mm, "construction": true});
            skPoint(sketch, "E181.visualSharp", {"position": v(-44.8, -4) * mm});
            skArc(sketch, "E181.filletArc", {"start": v(-42.69, -4.89) * mm, "mid": v(-44.4, -4.8) * mm, "end": v(-45.77, -5.82) * mm, "construction": true});
            skPoint(sketch, "E182.visualSharp", {"position": v(-44.8, 4) * mm});
            skArc(sketch, "E182.filletArc", {"start": v(-45.77, 5.82) * mm, "mid": v(-44.4, 4.8) * mm, "end": v(-42.69, 4.89) * mm, "construction": true});
            skPoint(sketch, "E183.visualSharp", {"position": v(-39.08, 6.38) * mm});
            skArc(sketch, "E183.filletArc", {"start": v(-41.64, 5.32) * mm, "mid": v(-40.19, 6.9) * mm, "end": v(-40.48, 9.04) * mm, "construction": true});
            skPoint(sketch, "E184.visualSharp", {"position": v(-48.1, 15.4) * mm});
            skArc(sketch, "E184.filletArc", {"start": v(-45.44, 14) * mm, "mid": v(-47.57, 14.3) * mm, "end": v(-49.16, 12.84) * mm, "construction": true});
            skPoint(sketch, "E185.visualSharp", {"position": v(-50.47, 9.68) * mm});
            skArc(sketch, "E185.filletArc", {"start": v(-49.6, 11.8) * mm, "mid": v(-49.68, 10.09) * mm, "end": v(-48.66, 8.71) * mm, "construction": true});
            skPoint(sketch, "E186.visualSharp", {"position": v(-58.5, 9.68) * mm});
            skArc(sketch, "E186.filletArc", {"start": v(-60.3, 8.71) * mm, "mid": v(-59.28, 10.09) * mm, "end": v(-59.37, 11.8) * mm});
            skPoint(sketch, "E187.visualSharp", {"position": v(-60.86, 15.4) * mm});
            skArc(sketch, "E187.filletArc", {"start": v(-59.8, 12.84) * mm, "mid": v(-61.4, 14.3) * mm, "end": v(-63.53, 14) * mm});
            skPoint(sketch, "E188.visualSharp", {"position": v(-69.88, 6.38) * mm});
            skArc(sketch, "E188.filletArc", {"start": v(-68.49, 9.04) * mm, "mid": v(-68.78, 6.9) * mm, "end": v(-67.32, 5.32) * mm});
            skPoint(sketch, "E189.visualSharp", {"position": v(-64.16, 4) * mm});
            skArc(sketch, "E189.filletArc", {"start": v(-66.28, 4.89) * mm, "mid": v(-64.57, 4.8) * mm, "end": v(-63.2, 5.82) * mm});
            skPoint(sketch, "E190.visualSharp", {"position": v(-64.16, -4) * mm});
            skArc(sketch, "E190.filletArc", {"start": v(-63.2, -5.82) * mm, "mid": v(-64.57, -4.8) * mm, "end": v(-66.28, -4.89) * mm});
            skPoint(sketch, "E191.visualSharp", {"position": v(-58.5, -9.68) * mm});
            skArc(sketch, "E191.filletArc", {"start": v(-59.37, -11.8) * mm, "mid": v(-59.28, -10.09) * mm, "end": v(-60.3, -8.71) * mm});
            skPoint(sketch, "E192.visualSharp", {"position": v(-60.86, -15.4) * mm});
            skArc(sketch, "E192.filletArc", {"start": v(-63.53, -14) * mm, "mid": v(-61.4, -14.3) * mm, "end": v(-59.8, -12.84) * mm});
            skPoint(sketch, "E193.visualSharp", {"position": v(-69.88, -6.38) * mm});
            skArc(sketch, "E193.filletArc", {"start": v(-67.32, -5.32) * mm, "mid": v(-68.78, -6.9) * mm, "end": v(-68.49, -9.04) * mm});
            skCircle(sketch, "E194", {"center": v(-111.68, 0) * mm, "radius": 10.48 * mm, "construction": true});
            skCircle(sketch, "E195", {"center": v(-111.68, 0) * mm, "radius": 16.67 * mm, "construction": true});
            skLineSegment(sketch, "E196", {"start": v(-105.3, 15.4) * mm, "end": v(-118.06, -15.4) * mm, "construction": true});
            skLineSegment(sketch, "E197", {"start": v(-118.06, 15.4) * mm, "end": v(-105.3, -15.4) * mm, "construction": true});
            skLineSegment(sketch, "E198", {"start": v(-127.08, 6.38) * mm, "end": v(-96.28, -6.38) * mm, "construction": true});
            skLineSegment(sketch, "E199", {"start": v(-96.28, 6.38) * mm, "end": v(-127.08, -6.38) * mm, "construction": true});
            skLineSegment(sketch, "E200", {"start": v(-128.35, 0) * mm, "end": v(-95.02, 0) * mm, "construction": true});
            skLineSegment(sketch, "E201", {"start": v(-116.57, -11.8) * mm, "end": v(-117, -12.84) * mm});
            skLineSegment(sketch, "E202", {"start": v(-123.48, -4.89) * mm, "end": v(-124.52, -5.32) * mm});
            skLineSegment(sketch, "E203", {"start": v(-123.48, 4.89) * mm, "end": v(-124.52, 5.32) * mm});
            skLineSegment(sketch, "E204", {"start": v(-116.57, 11.8) * mm, "end": v(-117, 12.84) * mm});
            skLineSegment(sketch, "E205", {"start": v(-106.8, 11.8) * mm, "end": v(-106.37, 12.84) * mm});
            skLineSegment(sketch, "E206", {"start": v(-99.89, 4.89) * mm, "end": v(-98.84, 5.32) * mm});
            skLineSegment(sketch, "E207", {"start": v(-101.2, 0) * mm, "end": v(-95.02, 0) * mm});
            skLineSegment(sketch, "E208", {"start": v(-99.89, -4.89) * mm, "end": v(-98.84, -5.32) * mm});
            skLineSegment(sketch, "E209", {"start": v(-106.8, -11.8) * mm, "end": v(-106.37, -12.84) * mm});
            skArc(sketch, "E210", {"start": v(-102.64, -14) * mm, "mid": v(-99.9, -11.79) * mm, "end": v(-97.68, -9.04) * mm});
            skArc(sketch, "E211", {"start": v(-97.68, 9.04) * mm, "mid": v(-99.9, 11.79) * mm, "end": v(-102.64, 14) * mm});
            skArc(sketch, "E212", {"start": v(-120.73, 14) * mm, "mid": v(-123.47, 11.79) * mm, "end": v(-125.69, 9.04) * mm});
            skArc(sketch, "E213", {"start": v(-125.69, -9.04) * mm, "mid": v(-123.47, -11.79) * mm, "end": v(-120.73, -14) * mm});
            skArc(sketch, "E214", {"start": v(-102.97, -5.82) * mm, "mid": v(-104.28, -7.4) * mm, "end": v(-105.86, -8.71) * mm});
            skArc(sketch, "E215", {"start": v(-117.5, -8.71) * mm, "mid": v(-119.1, -7.4) * mm, "end": v(-120.4, -5.82) * mm});
            skArc(sketch, "E216", {"start": v(-120.4, 5.82) * mm, "mid": v(-119.1, 7.4) * mm, "end": v(-117.5, 8.71) * mm});
            skArc(sketch, "E217", {"start": v(-105.86, 8.71) * mm, "mid": v(-104.28, 7.4) * mm, "end": v(-102.97, 5.82) * mm});
            skPoint(sketch, "E218.visualSharp", {"position": v(-107.67, -9.68) * mm});
            skArc(sketch, "E218.filletArc", {"start": v(-105.86, -8.71) * mm, "mid": v(-106.88, -10.09) * mm, "end": v(-106.8, -11.8) * mm});
            skPoint(sketch, "E219.visualSharp", {"position": v(-105.3, -15.4) * mm});
            skArc(sketch, "E219.filletArc", {"start": v(-106.37, -12.84) * mm, "mid": v(-104.77, -14.3) * mm, "end": v(-102.64, -14) * mm});
            skPoint(sketch, "E220.visualSharp", {"position": v(-96.28, -6.38) * mm});
            skArc(sketch, "E220.filletArc", {"start": v(-97.68, -9.04) * mm, "mid": v(-97.4, -6.9) * mm, "end": v(-98.84, -5.32) * mm});
            skPoint(sketch, "E221.visualSharp", {"position": v(-102, -4) * mm});
            skArc(sketch, "E221.filletArc", {"start": v(-99.89, -4.89) * mm, "mid": v(-101.6, -4.8) * mm, "end": v(-102.97, -5.82) * mm});
            skPoint(sketch, "E222.visualSharp", {"position": v(-102, 4) * mm});
            skArc(sketch, "E222.filletArc", {"start": v(-102.97, 5.82) * mm, "mid": v(-101.6, 4.8) * mm, "end": v(-99.89, 4.89) * mm});
            skPoint(sketch, "E223.visualSharp", {"position": v(-96.28, 6.38) * mm});
            skArc(sketch, "E223.filletArc", {"start": v(-98.84, 5.32) * mm, "mid": v(-97.4, 6.9) * mm, "end": v(-97.68, 9.04) * mm});
            skPoint(sketch, "E224.visualSharp", {"position": v(-105.3, 15.4) * mm});
            skArc(sketch, "E224.filletArc", {"start": v(-102.64, 14) * mm, "mid": v(-104.77, 14.3) * mm, "end": v(-106.37, 12.84) * mm});
            skPoint(sketch, "E225.visualSharp", {"position": v(-107.67, 9.68) * mm});
            skArc(sketch, "E225.filletArc", {"start": v(-106.8, 11.8) * mm, "mid": v(-106.88, 10.09) * mm, "end": v(-105.86, 8.71) * mm});
            skPoint(sketch, "E226.visualSharp", {"position": v(-115.7, 9.68) * mm});
            skArc(sketch, "E226.filletArc", {"start": v(-117.5, 8.71) * mm, "mid": v(-116.49, 10.09) * mm, "end": v(-116.57, 11.8) * mm});
            skPoint(sketch, "E227.visualSharp", {"position": v(-118.06, 15.4) * mm});
            skArc(sketch, "E227.filletArc", {"start": v(-117, 12.84) * mm, "mid": v(-118.6, 14.3) * mm, "end": v(-120.73, 14) * mm});
            skPoint(sketch, "E228.visualSharp", {"position": v(-127.08, 6.38) * mm});
            skArc(sketch, "E228.filletArc", {"start": v(-125.69, 9.04) * mm, "mid": v(-125.98, 6.9) * mm, "end": v(-124.52, 5.32) * mm});
            skPoint(sketch, "E229.visualSharp", {"position": v(-121.36, 4) * mm});
            skArc(sketch, "E229.filletArc", {"start": v(-123.48, 4.89) * mm, "mid": v(-121.77, 4.8) * mm, "end": v(-120.4, 5.82) * mm});
            skPoint(sketch, "E230.visualSharp", {"position": v(-121.36, -4) * mm});
            skArc(sketch, "E230.filletArc", {"start": v(-120.4, -5.82) * mm, "mid": v(-121.77, -4.8) * mm, "end": v(-123.48, -4.89) * mm});
            skPoint(sketch, "E231.visualSharp", {"position": v(-115.7, -9.68) * mm});
            skArc(sketch, "E231.filletArc", {"start": v(-116.57, -11.8) * mm, "mid": v(-116.49, -10.09) * mm, "end": v(-117.5, -8.71) * mm});
            skPoint(sketch, "E232.visualSharp", {"position": v(-118.06, -15.4) * mm});
            skArc(sketch, "E232.filletArc", {"start": v(-120.73, -14) * mm, "mid": v(-118.6, -14.3) * mm, "end": v(-117, -12.84) * mm});
            skPoint(sketch, "E233.visualSharp", {"position": v(-127.08, -6.38) * mm});
            skArc(sketch, "E233.filletArc", {"start": v(-124.52, -5.32) * mm, "mid": v(-125.98, -6.9) * mm, "end": v(-125.69, -9.04) * mm});
            skSolve(sketch);
        }
        {
            var Q0;
            Q0 = qSketchRegion(id + "F4", true);
            extrude(context, id + "F5", {"entities" : qUnion([Q0]), "operationType" : NewBodyOperationType.REMOVE, "endBound" : BoundingType.THROUGH_ALL, "oppositeDirection" : true, "depth" : 25.4 * mm, "offsetDistance" : 25.4 * mm});
        }
    });
